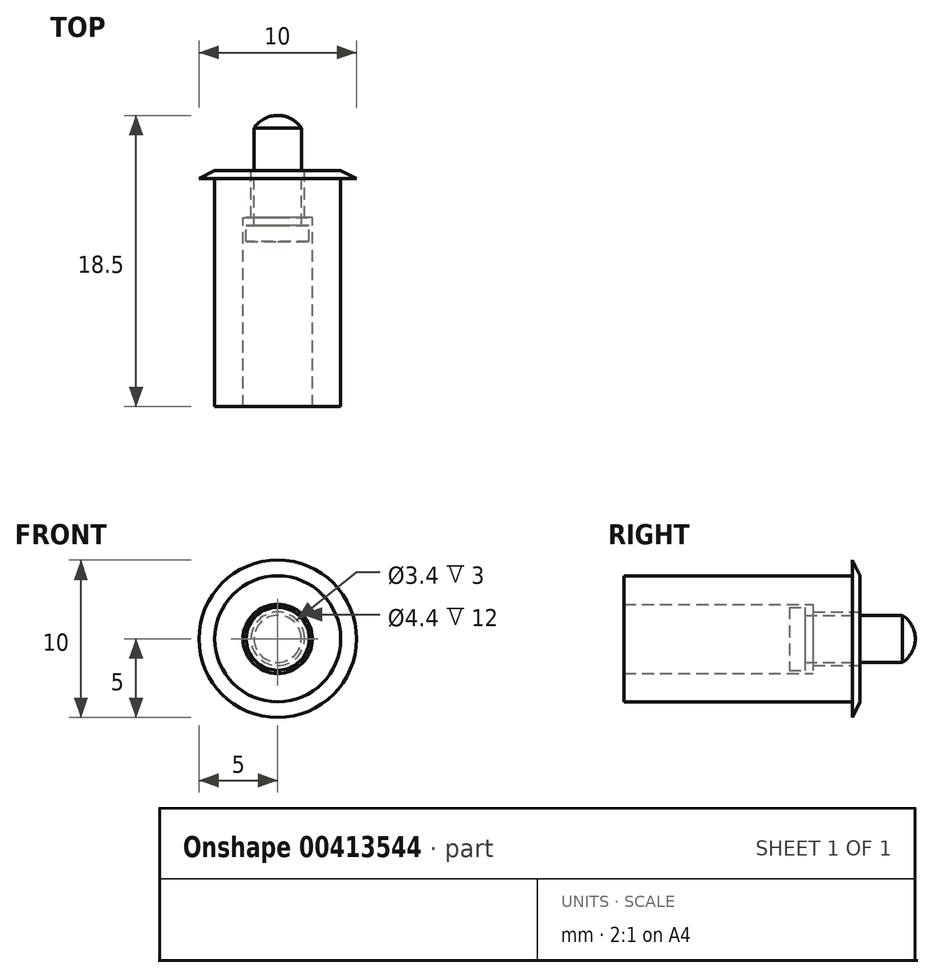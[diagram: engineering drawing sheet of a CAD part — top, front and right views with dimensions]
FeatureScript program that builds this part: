
annotation { "Feature Type Name" : "Feature", "Feature Type Description" : "" }
export const myFeature = defineFeature(function(context is Context, id is Id, definition is map)
    precondition{}
    {
        {
            var Q0;
            Q0=qCreatedBy(makeId("Top.planeOp"),FACE);
            var sketch = newSketch(context, id + "F0", { "sketchPlane" : qUnion([Q0])});
            skLineSegment(sketch, "E0.bottom", {"start": v(1.7, 135) * mm, "end": v(4, 135) * mm});
            skLineSegment(sketch, "E0.top", {"start": v(1.7, 132) * mm, "end": v(4, 132) * mm});
            skLineSegment(sketch, "E0.left", {"start": v(1.7, 135) * mm, "end": v(1.7, 132) * mm});
            skLineSegment(sketch, "E0.right", {"start": v(4, 135) * mm, "end": v(4, 132) * mm});
            skLineSegment(sketch, "E1.bottom", {"start": v(2.2, 132) * mm, "end": v(4, 132) * mm});
            skLineSegment(sketch, "E1.top", {"start": v(2.2, 120) * mm, "end": v(4, 120) * mm});
            skLineSegment(sketch, "E1.left", {"start": v(2.2, 132) * mm, "end": v(2.2, 120) * mm});
            skLineSegment(sketch, "E1.right", {"start": v(4, 132) * mm, "end": v(4, 120) * mm});
            skLineSegment(sketch, "E2", {"start": v(0, 73.1) * mm, "end": v(0, 61.83) * mm, "construction": true});
            skLineSegment(sketch, "E3.bottom", {"start": v(2, 131.5) * mm, "end": v(0, 131.5) * mm});
            skLineSegment(sketch, "E3.top", {"start": v(2, 130.5) * mm, "end": v(0, 130.5) * mm});
            skLineSegment(sketch, "E3.left", {"start": v(2, 131.5) * mm, "end": v(2, 130.5) * mm});
            skLineSegment(sketch, "E3.right", {"start": v(0, 131.5) * mm, "end": v(0, 130.5) * mm});
            skPoint(sketch, "E4", {"position": v(1.7, 131.5) * mm});
            skPoint(sketch, "E5", {"position": v(1.5, 131.5) * mm});
            skArc(sketch, "E6", {"start": v(1.5, 137.7) * mm, "mid": v(0, 138.5) * mm, "end": v(-1.5, 137.7) * mm});
            skLineSegment(sketch, "E7", {"start": v(0, 131.5) * mm, "end": v(0, 138.5) * mm});
            skLineSegment(sketch, "E8", {"start": v(1.5, 137.7) * mm, "end": v(1.5, 131.5) * mm});
            skLineSegment(sketch, "E9", {"start": v(4, 135) * mm, "end": v(5, 134.5) * mm});
            skLineSegment(sketch, "E10", {"start": v(5, 134.5) * mm, "end": v(4, 134.5) * mm});
            skSolve(sketch);
        }
        {
            var Q0;
            Q0=makeQuery(id+"F0.imprint","IMPRINT",FACE,{"disambiguationData":[TD([[makeQuery(id+"F0.imprint","IMPRINT",EDGE,{"derivedFrom":sQuery(id+"F0.wireOp",EDGE,"E1.top")}),1.0]])]});
            var Q1;
            Q1=makeQuery(id+"F0.imprint","IMPRINT",FACE,{"disambiguationData":[TD([[makeQuery(id+"F0.imprint","IMPRINT",EDGE,{"derivedFrom":sQuery(id+"F0.wireOp",EDGE,"E0.bottom")}),-1.0]])]});
            var Q2;
            {var subQ0=sQuery(id+"F0.wireOp",EDGE,"E7");Q2=makeQuery(id+"F0.imprint","IMPRINT",FACE,{"disambiguationData":[TD([[makeQuery(id+"F0.imprint","IMPRINT",EDGE,{"derivedFrom":subQ0}),-1.0]])]});}
            var Q3;
            {var subQ0=sQuery(id+"F0.wireOp",EDGE,"E9");Q3=makeQuery(id+"F0.imprint","IMPRINT",FACE,{"disambiguationData":[TD([[makeQuery(id+"F0.imprint","IMPRINT",EDGE,{"derivedFrom":subQ0}),-1.0]])]});}
            var Q4;
            Q4=makeQuery(id+"F0.imprint","IMPRINT",FACE,{"disambiguationData":[TD([[makeQuery(id+"F0.imprint","IMPRINT",EDGE,{"derivedFrom":sQuery(id+"F0.wireOp",EDGE,"E3.top")}),-1.0]])]});
            var Q5;
            Q5=sQuery(id+"F0.wireOp",EDGE,"E2");
            revolve(context, id + "F1", {"entities" : qUnion([Q0, Q1, Q2, Q3, Q4]), "axis" : qUnion([Q5]), "revolveType" : RevolveType.FULL});
        }
    });
